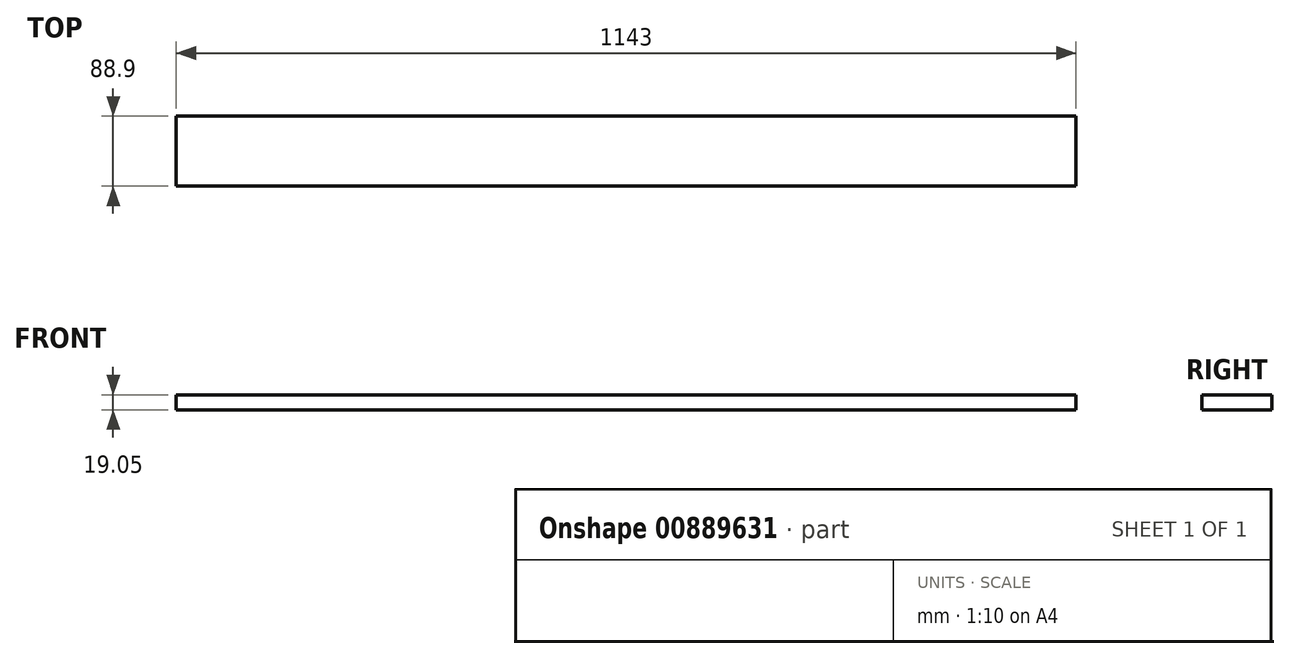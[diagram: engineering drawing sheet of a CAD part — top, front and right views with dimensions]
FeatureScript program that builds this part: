
annotation { "Feature Type Name" : "Feature", "Feature Type Description" : "" }
export const myFeature = defineFeature(function(context is Context, id is Id, definition is map)
    precondition{}
    {
        {
            var Q0;
            Q0=qCreatedBy(makeId("Top.planeOp"),FACE);
            var sketch = newSketch(context, id + "F0", { "sketchPlane" : qUnion([Q0])});
            skLineSegment(sketch, "E0.bottom", {"start": v(0, 0) * mm, "end": v(1143, 0) * mm});
            skLineSegment(sketch, "E0.top", {"start": v(0, 88.9) * mm, "end": v(1143, 88.9) * mm});
            skLineSegment(sketch, "E0.left", {"start": v(0, 0) * mm, "end": v(0, 88.9) * mm});
            skLineSegment(sketch, "E0.right", {"start": v(1143, 0) * mm, "end": v(1143, 88.9) * mm});
            skSolve(sketch);
        }
        {
            var Q0;
            Q0 = qSketchRegion(id + "F0", true);
            extrude(context, id + "F1", {"entities" : qUnion([Q0]), "depth" : 19.05 * mm, "offsetDistance" : 25.4 * mm});
        }
    });
